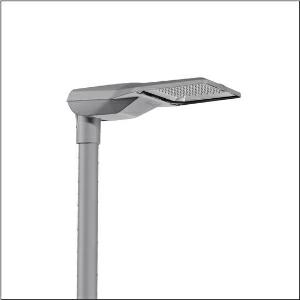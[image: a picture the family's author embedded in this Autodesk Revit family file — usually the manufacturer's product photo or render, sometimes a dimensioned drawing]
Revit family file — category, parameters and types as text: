
# Revit family: streetlight_sl_21_iq_midi___stw1_0a_5xe3e41g08mb_cdbd
name_source: partatom
category: Lighting Fixtures
units: mm (PartAtom-declared; Revit-internal decimal feet)

## family parameters
Cut with Voids When Loaded = No
Host = Face
Light Source = No
Part Type = Normal
Room Calculation Point = No
Round Connector Dimension = Use Diameter
Shared = No

## types (1)
- --- (1 x LED, 20360 lm, 146.7 W, 4000K)
    Apparent Load = 147 VA
    CIE Flux Codes = 38 75 98 100 100
    Color Rendering = 70
    Color Temperature = 4000K
    Default Elevation = 1800 mm
    Description = Streetlight SL 21 iQ midi, mast luminaire, primary light control with lens, of PMMA, primary optical cover: cover, of toughened safety glass, transparent, light distribution: STW1.0a, light emission: direct distribution, primary light characteristic: asymmetric, installation type: post-top, side-entry, LED, High Power LED, rated luminous flux: 20.360lm, luminous efficacy: 139lm/W, light colour: 740, colour temperature: 4000K, control: Street-Remote, Auto-Match, Temp-Guard, Lumen-Switch, Night-Set, Smart-Wire, Light-Fading, Desk-Remote (wireless, voltage-free reading and setting of iQ features in the workshop via application-optimized NFC function/RFID function), optimised constant luminous flux control (CLO 2.0), presetting dimming linear, mains connection: 230..240V, AC, 50/60Hz, start of lifetime: 147W, end of service life: 161W, reduction: 62W, luminaire housing, of diecast aluminium, powder-coated, Siteco® metallic grey (DB 702S), corrosivity category C5 mid according to DIN EN ISO 12944, please order mast flange separately, inclination adjustable: 0°, 5°, 10°, 15°, sealing non-destructively replaceable, multi-level sealing system, length: 644mm, width: 335mm, height: 110mm, mast flange for spigot size: 42mm (side-entry): 5XC10008XM4, 60/48mm (side-entry/post-top): 5XC10108XM2, 76/60mm (side-entry/post-top): 5XC10108XM1, protection rating (complete): IP66, insulation class (complete): insulation class II (safety insulation), certification: CE, ENEC, ENEC+, VDE, impact resistance: IK09, permissible operating ambient temperature for outdoor applications: -40..+50°C, standard-compliant lighting for roads and squares, packaging unit: 1 piece

Light Distribution: STW1.0a
    Height = 111 mm
    Lamp = 1 x LED
    Lamp Light Flux = 20360 lm
    Lamp Power = 146.7 W
    Lamp count = 1
    Length = 644 mm
    Luminous efficacy = 139 lm/W
    Manufacturer = Siteco
    ModVariant = No
    Model = 5XE3E41G08MB
    Number of Poles = 1
    OnlyDefault = Yes
    Power Factor = 1
    Product Name = Streetlight SL 21 iQ midi | STW1.0a
    Product group = mast luminaire | pylon top
    ProductGroupID = 6100
    Protection Class = Protection class II
    Protection Degree = IP 66
    RLX_Detail_Level = 1
    RLX_Emergency_Light_Flux = 0 lm
    RLX_Emergency_Type = 0
    RLX_Emergency_Type_DB = No
    RlxData = <blob elided: 90581 chars, md5=fb2c6680>
    Socket = socket
    Standby Power = 0 W
    System Light Flux = 20360 lm
    System Power = 147 W
    Type Comments = factory setting: luminous flux: 100 % | dim-lin: 254 | 753 mA
    Type Image = l_1004298.jpg
    URL = http://relux.com
    VarID = @adj_121749
    Voltage = 0 V
    Weight = 0.00 kg
    Width = 336 mm

## geometry (parser evidence)
native form markers: Blend x4, Sweep x13
no freeform markers — native parametric forms only
